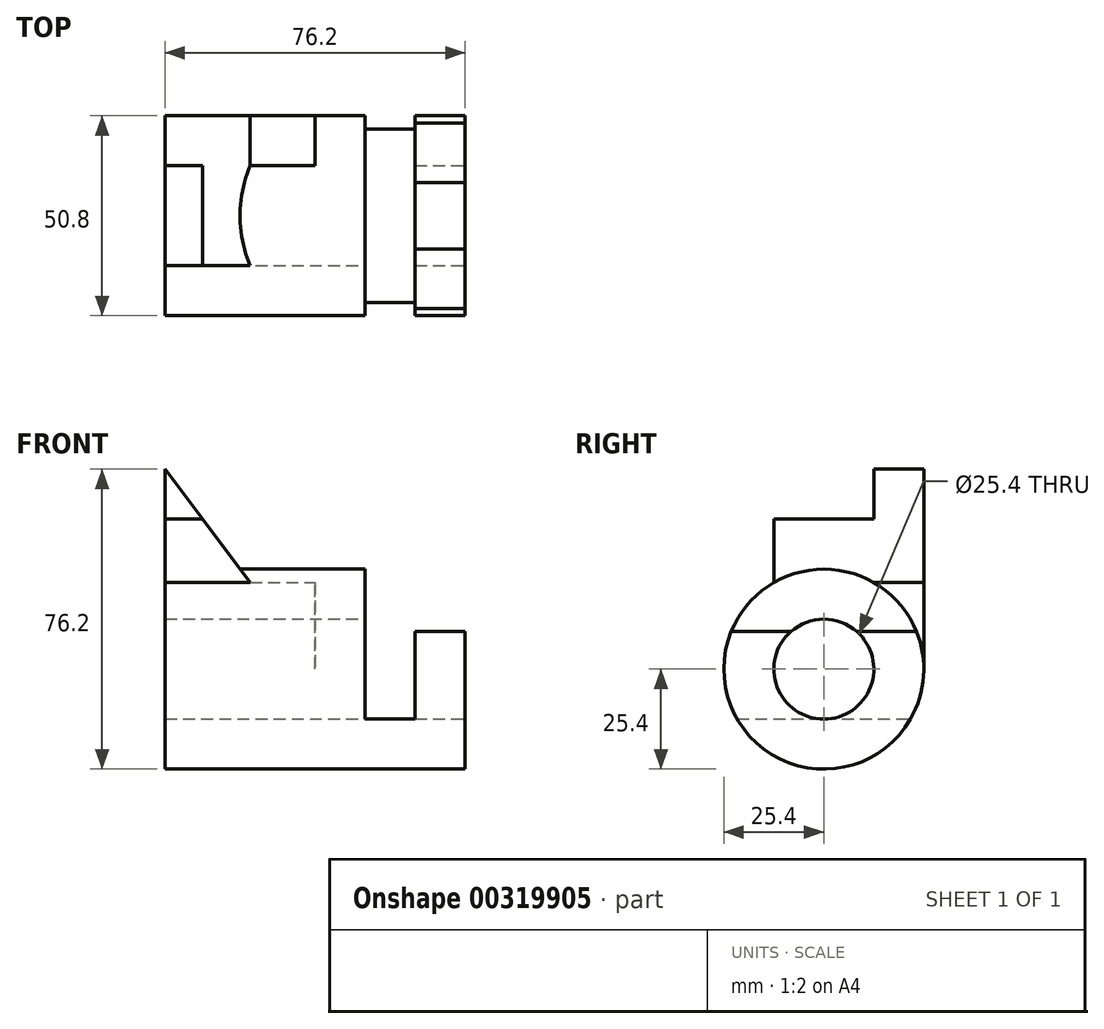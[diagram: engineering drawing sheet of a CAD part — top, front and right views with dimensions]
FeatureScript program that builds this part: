
annotation { "Feature Type Name" : "Feature", "Feature Type Description" : "" }
export const myFeature = defineFeature(function(context is Context, id is Id, definition is map)
    precondition{}
    {
        {
            var Q0;
            Q0=qCreatedBy(makeId("Front.planeOp"),FACE);
            var sketch = newSketch(context, id + "F0", { "sketchPlane" : qUnion([Q0])});
            skLineSegment(sketch, "E0", {"start": v(0, 0) * mm, "end": v(76.2, 0) * mm});
            skLineSegment(sketch, "E1", {"start": v(0, 0) * mm, "end": v(0, 76.2) * mm});
            skLineSegment(sketch, "E2", {"start": v(0, 76.2) * mm, "end": v(76.2, 76.2) * mm});
            skLineSegment(sketch, "E3", {"start": v(76.2, 76.2) * mm, "end": v(76.2, 0) * mm});
            skSolve(sketch);
        }
        {
            var Q0;
            Q0 = qSketchRegion(id + "F0", true);
            extrude(context, id + "F1", {"entities" : qUnion([Q0]), "depth" : 50.8 * mm});
        }
        {
            var Q0;
            Q0=makeQuery(id+"F1.opExtrude","SWEPT_FACE",FACE,{"disambiguationData":[OSD([sQuery(id+"F0.wireOp",EDGE,"E3")])]});
            var sketch = newSketch(context, id + "F2", { "sketchPlane" : qUnion([Q0])});
            skLineSegment(sketch, "E4", {"start": v(-25.4, 0) * mm, "end": v(-25.4, 50.8) * mm, "construction": true});
            skPoint(sketch, "E5", {"position": v(-50.8, 25.4) * mm});
            skLineSegment(sketch, "E6", {"start": v(-50.8, 25.4) * mm, "end": v(0, 25.4) * mm, "construction": true});
            skCircle(sketch, "E7", {"center": v(-25.4, 25.4) * mm, "radius": 12.7 * mm});
            skCircle(sketch, "E8", {"center": v(-25.4, 25.4) * mm, "radius": 25.4 * mm});
            skPoint(sketch, "E9", {"position": v(-25.4, 34.93) * mm});
            skLineSegment(sketch, "E10", {"start": v(-33.8, 34.93) * mm, "end": v(-48.95, 34.93) * mm});
            skLineSegment(sketch, "E11", {"start": v(-17, 34.93) * mm, "end": v(-1.85, 34.93) * mm});
            skLineSegment(sketch, "E12", {"start": v(0, 76.2) * mm, "end": v(-12.7, 76.2) * mm});
            skLineSegment(sketch, "E13", {"start": v(-12.7, 76.2) * mm, "end": v(-12.7, 63.5) * mm});
            skLineSegment(sketch, "E14", {"start": v(0, 76.2) * mm, "end": v(0, 25.4) * mm});
            skLineSegment(sketch, "E15", {"start": v(-12.7, 63.5) * mm, "end": v(-38.1, 63.5) * mm});
            skLineSegment(sketch, "E16", {"start": v(-38.1, 63.5) * mm, "end": v(-38.1, 47.4) * mm});
            skSolve(sketch);
        }
        {
            var Q0;
            {var subQ0=sQuery(id+"F2.wireOp",EDGE,"E13");Q0=makeQuery(id+"F2.imprint","IMPRINT",FACE,{"disambiguationData":[TD([[makeQuery(id+"F2.imprint","IMPRINT",EDGE,{"derivedFrom":subQ0}),-1.0]])]});}
            var Q1;
            {var subQ0=sQuery(id+"F2.wireOp",EDGE,"E8");var subQ1=sQuery(id+"F0.wireOp",EDGE,"E3");var subQ2=makeQuery(id+"F1.opExtrude","CAP_EDGE",EDGE,{"disambiguationData":[OSD([subQ1])],"isStart":false});var subQ3=makeQuery(id+"F2.imprint","INTERSECT",VERTEX,{"derivedFrom":[subQ2,subQ0]});Q1=makeQuery(id+"F2.imprint","IMPRINT",FACE,{"disambiguationData":[TD([[makeQuery(id+"F2.imprint","IMPRINT",EDGE,{"disambiguationData":[TD([[subQ3,-1.0]])],"derivedFrom":subQ0}),-1.0]])]});}
            var Q2;
            {var subQ0=sQuery(id+"F2.wireOp",EDGE,"E8");var subQ1=sQuery(id+"F0.wireOp",EDGE,"E3");var subQ2=makeQuery(id+"F1.opExtrude","CAP_EDGE",EDGE,{"disambiguationData":[OSD([subQ1])],"isStart":true});var subQ3=makeQuery(id+"F2.imprint","INTERSECT",VERTEX,{"derivedFrom":[subQ2,subQ0,sQuery(id+"F2.wireOp",EDGE,"E14")]});Q2=makeQuery(id+"F2.imprint","IMPRINT",FACE,{"disambiguationData":[TD([[makeQuery(id+"F2.imprint","IMPRINT",EDGE,{"disambiguationData":[TD([[subQ3,1.0]])],"derivedFrom":subQ0}),-1.0]])]});}
            var Q3;
            {var subQ0=sQuery(id+"F2.wireOp",EDGE,"E7");var subQ1=makeQuery(id+"F2.imprint","INTERSECT",VERTEX,{"derivedFrom":[subQ0,sQuery(id+"F2.wireOp",EDGE,"E10")]});Q3=makeQuery(id+"F2.imprint","IMPRINT",FACE,{"disambiguationData":[TD([[makeQuery(id+"F2.imprint","IMPRINT",EDGE,{"disambiguationData":[TD([[subQ1,1.0]])],"derivedFrom":subQ0}),1.0]])]});}
            extrude(context, id + "F3", {"entities" : qUnion([Q0, Q1, Q2, Q3]), "operationType" : NewBodyOperationType.REMOVE, "endBound" : BoundingType.THROUGH_ALL, "oppositeDirection" : true, "depth" : 25.4 * mm});
        }
        {
            var Q0;
            Q0=makeQuery(id+"F2.imprint","IMPRINT",FACE,{"disambiguationData":[TD([[makeQuery(id+"F2.imprint","IMPRINT",EDGE,{"derivedFrom":sQuery(id+"F2.wireOp",EDGE,"E12")}),-1.0]])]});
            extrude(context, id + "F4", {"entities" : qUnion([Q0]), "operationType" : NewBodyOperationType.REMOVE, "oppositeDirection" : true, "depth" : 38.1 * mm});
        }
        {
            var Q0;
            Q0=qCreatedBy(makeId("Front.planeOp"),FACE);
            var sketch = newSketch(context, id + "F5", { "sketchPlane" : qUnion([Q0])});
            skLineSegment(sketch, "E17", {"start": v(76.2, 34.93) * mm, "end": v(76.2, 0) * mm});
            skLineSegment(sketch, "E18", {"start": v(76.2, 34.93) * mm, "end": v(63.5, 34.93) * mm});
            skLineSegment(sketch, "E19", {"start": v(63.5, 34.93) * mm, "end": v(63.5, 12.7) * mm});
            skLineSegment(sketch, "E20", {"start": v(63.5, 12.7) * mm, "end": v(50.8, 12.7) * mm});
            skLineSegment(sketch, "E21", {"start": v(50.8, 12.7) * mm, "end": v(50.8, 50.8) * mm});
            skLineSegment(sketch, "E22", {"start": v(50.8, 50.8) * mm, "end": v(0, 50.8) * mm});
            skLineSegment(sketch, "E23", {"start": v(0, 50.8) * mm, "end": v(0, 0) * mm});
            skLineSegment(sketch, "E24", {"start": v(0, 0) * mm, "end": v(76.2, 0) * mm});
            skLineSegment(sketch, "E25", {"start": v(50.8, 50.8) * mm, "end": v(76.2, 50.8) * mm});
            skLineSegment(sketch, "E26", {"start": v(76.2, 50.8) * mm, "end": v(76.2, 0) * mm});
            skLineSegment(sketch, "E27", {"start": v(76.2, 0) * mm, "end": v(76.2, 50.8) * mm});
            skSolve(sketch);
        }
        {
            var Q0;
            {var subQ0=sQuery(id+"F5.wireOp",EDGE,"E18");Q0=makeQuery(id+"F5.imprint","IMPRINT",FACE,{"disambiguationData":[TD([[makeQuery(id+"F5.imprint","IMPRINT",EDGE,{"derivedFrom":subQ0}),-1.0]])]});}
            extrude(context, id + "F6", {"entities" : qUnion([Q0]), "operationType" : NewBodyOperationType.REMOVE, "endBound" : BoundingType.THROUGH_ALL, "depth" : 25.4 * mm});
        }
        {
            var Q0;
            Q0=makeQuery(id+"F0.imprint","IMPRINT",FACE,{"disambiguationData":[TD([[makeQuery(id+"F0.imprint","IMPRINT",EDGE,{"derivedFrom":sQuery(id+"F0.wireOp",EDGE,"E0")}),1.0]])]});
            var sketch = newSketch(context, id + "F7", { "sketchPlane" : qUnion([Q0])});
            skLineSegment(sketch, "E28", {"start": v(0, 0) * mm, "end": v(0, 25.4) * mm});
            skLineSegment(sketch, "E29", {"start": v(0, 25.4) * mm, "end": v(38.1, 25.4) * mm, "construction": true});
            skLineSegment(sketch, "E30", {"start": v(0, 25.4) * mm, "end": v(0, 76.2) * mm, "construction": true});
            skLineSegment(sketch, "E31", {"start": v(0, 76.2) * mm, "end": v(38.1, 25.4) * mm, "construction": true});
            skLineSegment(sketch, "E32", {"start": v(0, 76.2) * mm, "end": v(0, 47.4) * mm});
            skLineSegment(sketch, "E33", {"start": v(0, 47.4) * mm, "end": v(21.6, 47.4) * mm});
            skLineSegment(sketch, "E34", {"start": v(21.6, 47.4) * mm, "end": v(0, 76.2) * mm});
            skLineSegment(sketch, "E35", {"start": v(21.6, 47.4) * mm, "end": v(38.1, 47.4) * mm});
            skLineSegment(sketch, "E36", {"start": v(38.1, 47.4) * mm, "end": v(38.1, 76.2) * mm});
            skLineSegment(sketch, "E37", {"start": v(0, 76.2) * mm, "end": v(38.1, 76.2) * mm});
            skSolve(sketch);
        }
        {
            var Q0;
            Q0=makeQuery(id+"F7.imprint","IMPRINT",FACE,{"disambiguationData":[TD([[makeQuery(id+"F7.imprint","IMPRINT",EDGE,{"derivedFrom":sQuery(id+"F7.wireOp",EDGE,"E34")}),-1.0]])]});
            extrude(context, id + "F8", {"entities" : qUnion([Q0]), "operationType" : NewBodyOperationType.REMOVE, "endBound" : BoundingType.THROUGH_ALL, "depth" : 25.4 * mm});
        }
        {
            var Q0;
            Q0=makeQuery(id+"F6.boolean.opBoolean","COPY",FACE,{"derivedFrom":makeQuery(id+"F6.opExtrude","SWEPT_FACE",FACE,{"disambiguationData":[OSD([sQuery(id+"F5.wireOp",EDGE,"E21")])]})});
            var sketch = newSketch(context, id + "F9", { "sketchPlane" : qUnion([Q0])});
            skPoint(sketch, "E38", {"position": v(-48.95, 34.93) * mm});
            skPoint(sketch, "E39", {"position": v(-1.85, 34.93) * mm});
            skArc(sketch, "E40", {"start": v(-1.85, 34.93) * mm, "mid": v(-25.4, 50.8) * mm, "end": v(-48.95, 34.92) * mm});
            skLineSegment(sketch, "E41", {"start": v(-1.85, 34.93) * mm, "end": v(-17, 34.93) * mm});
            skLineSegment(sketch, "E42", {"start": v(-48.95, 34.93) * mm, "end": v(-33.8, 34.93) * mm});
            skArc(sketch, "E43", {"start": v(-17, 34.93) * mm, "mid": v(-25.4, 38.1) * mm, "end": v(-33.8, 34.93) * mm});
            skSolve(sketch);
        }
        {
            var Q0;
            Q0 = qSketchRegion(id + "F9", true);
            extrude(context, id + "F10", {"entities" : qUnion([Q0]), "operationType" : NewBodyOperationType.ADD, "oppositeDirection" : true, "depth" : 50.8 * mm});
        }
    });
